# Revit family: Haworth_Planes_TrainingTable_Pie
name_source: partatom
category: Furniture Systems
revit_build: Autodesk Revit 2018 (Build: 20170223_1515(x64)
units: mm (PartAtom-declared; Revit-internal decimal feet)

## family parameters
Always vertical = Yes
Cut with Voids When Loaded = No
OmniClass Number = 23.40.70.14.64.21
OmniClass Title = Systems Furniture
Part Type = Normal
Room Calculation Point = No
Round Connector Dimension = Use Diameter
Shared = No
Work Plane-Based = No

## types (3) — shared parameters
15 Degrees = No
30 Degrees = No
45 Degrees = No
90 Degrees = Yes
Actual Angle = 90.00°
Angle Half = 45.00°
Assembly Code = E2020200
Custom Size = No
Height = 29"
Manufacturer = Haworth
Max Angle = 90.00°
Max Depth = 30"
Min Angle = 15.00°
Min Depth = 20"
Model = TAPC
Revision Number = 2
Size = Verify Final Dim. w/ Haworth
Standard Angles = 15, 30, 45, 90 degrees
Standard Depths = 20, 24, 30 inches
Sustainability Info = http://media.haworth.com
URL = www.haworth.com
URL - Product = http://www.haworth.com
Warranty = http://www.haworth.com
Worksurface Thickness = 1 3/16"

## per-type parameters (varying)
| type | Actual Depth | Depth | Description |
| 24d | 24" | 24" | Haworth - Planes Training - Table Pie - 24d |
| 20d | 20" | 20" | Haworth - Planes Training - Table Pie - 20d |
| 30d | 30" | 30" | Haworth - Planes Training - Table Pie - 30d |

## geometry (parser evidence)
native form markers: Sweep x3
no freeform markers — native parametric forms only
